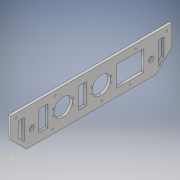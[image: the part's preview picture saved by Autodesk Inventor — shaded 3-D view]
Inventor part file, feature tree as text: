
AUTODESK INVENTOR PART (.ipt)
format: ipt  version: 2017 (Build 210142000, 142)  size: 301,056 bytes
history: native  units: in
note: dims shown in document units (in); Inventor stores cm internally (conversion verified against a paired STEP export)
features: sketch x15, hole x8, extrude x7, chamfer x3, thicken_offset x1, projected_geometry x1
ambient origin geometry x8: Origin, YZ Plane, XZ Plane, XY Plane, X Axis, Y Axis, Z Axis, Center Point
bodies: Solid1 (feature_tree)
feature tree (35):
  extrude  "Extrusion1"  Depth=15.5in
  sketch  "Sketch3"  dims[d4=2.0in]
  sketch  "Sketch4"  dims[d5=1.0in]
  chamfer  "Chamfer1"  Distance=0.25in
  chamfer  "Chamfer2"  Distance=1.5in Angle=45.0deg
  hole  "Hole1"  [1 undecoded]
  hole  "Hole3"  [1 undecoded]
  sketch  "Sketch8"  dims[d13=1.5in d14=0.125in d15=45.0deg d16=2.0in]
  hole  "Hole4"  [1 undecoded]
  hole  "Hole6"  [1 undecoded]
  extrude  "Extrusion2"  Depth=0.5in
  thicken_offset  "Thicken1"
  sketch  "Sketch16"  dims[d20=0.501in d21=0.75in d22=0.375in d23=0.25in d24=0.5635in d25=1.0in d26=0.8108in d42=0.394in]
  sketch  "Sketch17"  dims[d43=3.75in d44=3.75in]
  sketch  "Sketch18"  dims[d45=0.144in d46=0.5in]
  hole  "Hole10"  [1 undecoded]
  hole  "Hole11"  [1 undecoded]
  hole  "Hole12"  [1 undecoded]
  hole  "Hole13"  [1 undecoded]
  sketch  "Sketch19"  dims[d47=0.5in]
  sketch  "Sketch20"  dims[d48=0.188in d49=0.75in d50=0.375in d51=0.25in d52=0.5635in d53=1.0in d54=0.8108in d57=0.394in]
  extrude  "Extrusion3"  Depth=0.75in
  extrude  "Extrusion4"  Depth=0.75in
  sketch  "Sketch21"  dims[d61=0.14in d62=0.75in d63=0.375in d64=0.25in d65=0.5635in d66=1.0in d67=0.8108in]
  extrude  "Extrusion5"  Depth=0.75in
  extrude  "Extrusion6"  Depth=0.75in
  extrude  "Extrusion7"  Depth=0.75in
  chamfer  "Chamfer5"  Distance=0.945in
  sketch  "Sketch1"  dims[d2=3.25in d3=15.5in]
  sketch  "Sketch5"  dims[d6=2.0in]
  projected_geometry  "Projected Loop1"
  sketch  "Sketch7"  dims[d7=1.0in d8=0.25in d9=0.0in d10=1.5in d11=0.125in d12=45.0deg]
  sketch  "Sketch10"  dims[d17=1.5in d18=1.5in]
  sketch  "Sketch14"  dims[d19=2.0in]
  sketch  "Sketch22"  dims[d75=1.7in d76=0.75in d77=0.375in d78=0.25in d79=0.5635in d80=1.0in d81=0.8108in d82=0.144in d108=1.5in d109=1.5in d113=0.945in d114=0.276in d115=0.276in d116=0.945in d117=0.945in d118=0.945in d119=0.138in d120=0.138in d121=0.138in d122=0.138in d123=0.138in d124=1.0in d125=0.0in d128=8.75in d129=0.25in d130=0.25in d131=0.4in d132=0.4in d133=3.0in d135=0.14in d136=3.5in d138=0.14in d139=0.394in d141=4.0in d143=4.0in d145=0.188in d146=0.188in d147=0.14in d148=0.75in d149=0.375in d150=0.25in d151=0.5635in d152=1.0in d153=0.8108in d154=0.14in d155=0.75in d156=0.375in d157=0.25in d158=0.5635in d159=1.0in d160=0.8108in d161=0.14in d162=0.75in d163=0.375in d164=0.25in d165=0.5635in d166=1.0in d167=0.8108in d168=0.14in d169=0.75in d170=0.375in d171=0.25in d172=0.5635in d173=1.0in d174=0.8108in d183=0.75in d184=0.75in d185=0.75in d186=0.45in d187=0.45in d188=0.45in d189=0.45in d190=0.75in d191=1.0in d192=0.0in d193=1.0in d194=0.0in d195=0.75in d196=0.45in d197=0.45in d198=0.75in d199=0.75in d200=0.75in d201=0.45in d202=0.45in d203=1.0in d204=0.0in d205=1.0in d206=0.0in d207=0.75in d208=0.45in d209=0.75in d210=1.0in d211=0.0in d212=0.125in d213=0.125in d214=45.0deg d177=1.0in d178=1.0in]
note: 8 required parameter values undecoded (feature->parameter linkage not recoverable at this tier; creation-order binding heuristic only, values carry confidence <= 0.55)
